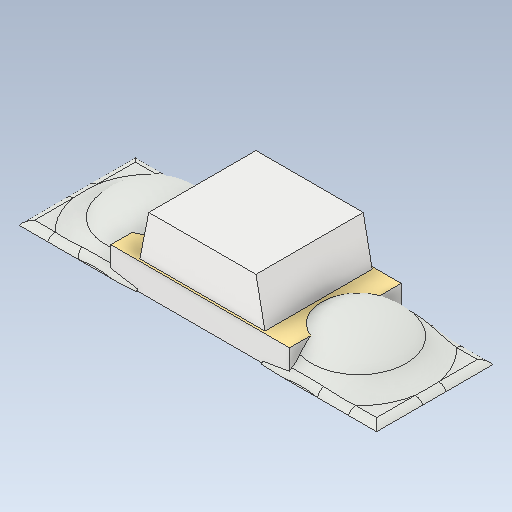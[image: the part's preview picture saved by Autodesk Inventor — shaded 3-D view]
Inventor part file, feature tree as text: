
AUTODESK INVENTOR PART (.ipt)
format: ipt  version: 2020.1 (Build 241239000, 239)  size: 225,792 bytes
history: native  units: mm
features: mirror x1, other x1
ambient origin geometry x8: Origin, YZ Plane, XZ Plane, XY Plane, X Axis, Y Axis, Z Axis, Center Point
bodies: Solid1 (feature_tree), Solid2 (feature_tree)
feature tree (2):
  mirror  "Mirror3"
  other  "Boss-Extrude5"
